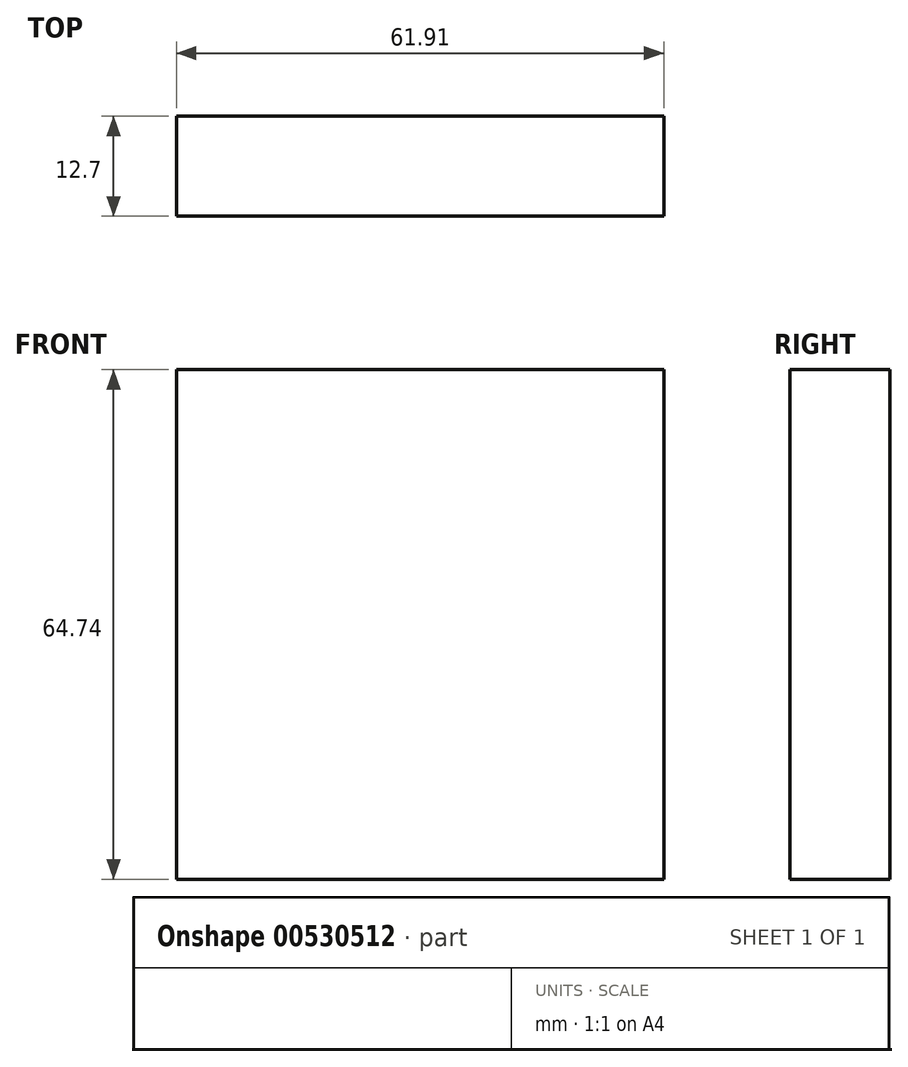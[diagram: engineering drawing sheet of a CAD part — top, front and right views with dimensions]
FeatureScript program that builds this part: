
annotation { "Feature Type Name" : "Feature", "Feature Type Description" : "" }
export const myFeature = defineFeature(function(context is Context, id is Id, definition is map)
    precondition{}
    {
        {
            var Q0;
            Q0=qCreatedBy(makeId("Front.planeOp"),FACE);
            var sketch = newSketch(context, id + "F0", { "sketchPlane" : qUnion([Q0])});
            skLineSegment(sketch, "E0", {"start": v(-38, 26.54) * mm, "end": v(-38, -38.2) * mm});
            skLineSegment(sketch, "E1", {"start": v(-38, -38.2) * mm, "end": v(23.92, -38.2) * mm});
            skLineSegment(sketch, "E2", {"start": v(23.92, -38.2) * mm, "end": v(23.92, 26.54) * mm});
            skLineSegment(sketch, "E3", {"start": v(23.92, 26.54) * mm, "end": v(-38, 26.54) * mm});
            skSolve(sketch);
        }
        {
            var Q0;
            Q0=makeQuery(id+"F0.imprint","IMPRINT",FACE,{"disambiguationData":[TD([[makeQuery(id+"F0.imprint","IMPRINT",EDGE,{"derivedFrom":sQuery(id+"F0.wireOp",EDGE,"E0")}),1.0]])]});
            extrude(context, id + "F1", {"entities" : qUnion([Q0]), "depth" : 25.4 * mm, "offsetDistance" : 25.4 * mm});
        }
        {
            var Q0;
            Q0=makeQuery(id+"F1.opExtrude","CAP_FACE",FACE,{"disambiguationData":[OSD([sQuery(id+"F0.wireOp",EDGE,"E0"),sQuery(id+"F0.wireOp",EDGE,"E1"),sQuery(id+"F0.wireOp",EDGE,"E2"),sQuery(id+"F0.wireOp",EDGE,"E3")])],"isStart":false});
            var sketch = newSketch(context, id + "F2", { "sketchPlane" : qUnion([Q0])});
            skLineSegment(sketch, "E4", {"start": v(-19.94, 26.54) * mm, "end": v(-19.94, -26.72) * mm});
            skLineSegment(sketch, "E5", {"start": v(-19.94, -26.72) * mm, "end": v(23.92, -26.72) * mm});
            skSolve(sketch);
        }
        {
            var Q0;
            Q0=makeQuery(id+"F1.opExtrude","CAP_FACE",FACE,{"disambiguationData":[OSD([sQuery(id+"F0.wireOp",EDGE,"E0"),sQuery(id+"F0.wireOp",EDGE,"E1"),sQuery(id+"F0.wireOp",EDGE,"E2"),sQuery(id+"F0.wireOp",EDGE,"E3")])],"isStart":false});
            var Q1;
            {var subQ0=sQuery(id+"F2.wireOp",EDGE,"E4");Q1=makeQuery(id+"F2.imprint","IMPRINT",FACE,{"disambiguationData":[TD([[makeQuery(id+"F2.imprint","IMPRINT",EDGE,{"derivedFrom":subQ0}),1.0]])]});}
            extrude(context, id + "F3", {"entities" : qUnion([Q0, Q1]), "operationType" : NewBodyOperationType.REMOVE, "oppositeDirection" : true, "depth" : 12.7 * mm, "offsetDistance" : 25.4 * mm});
        }
    });
